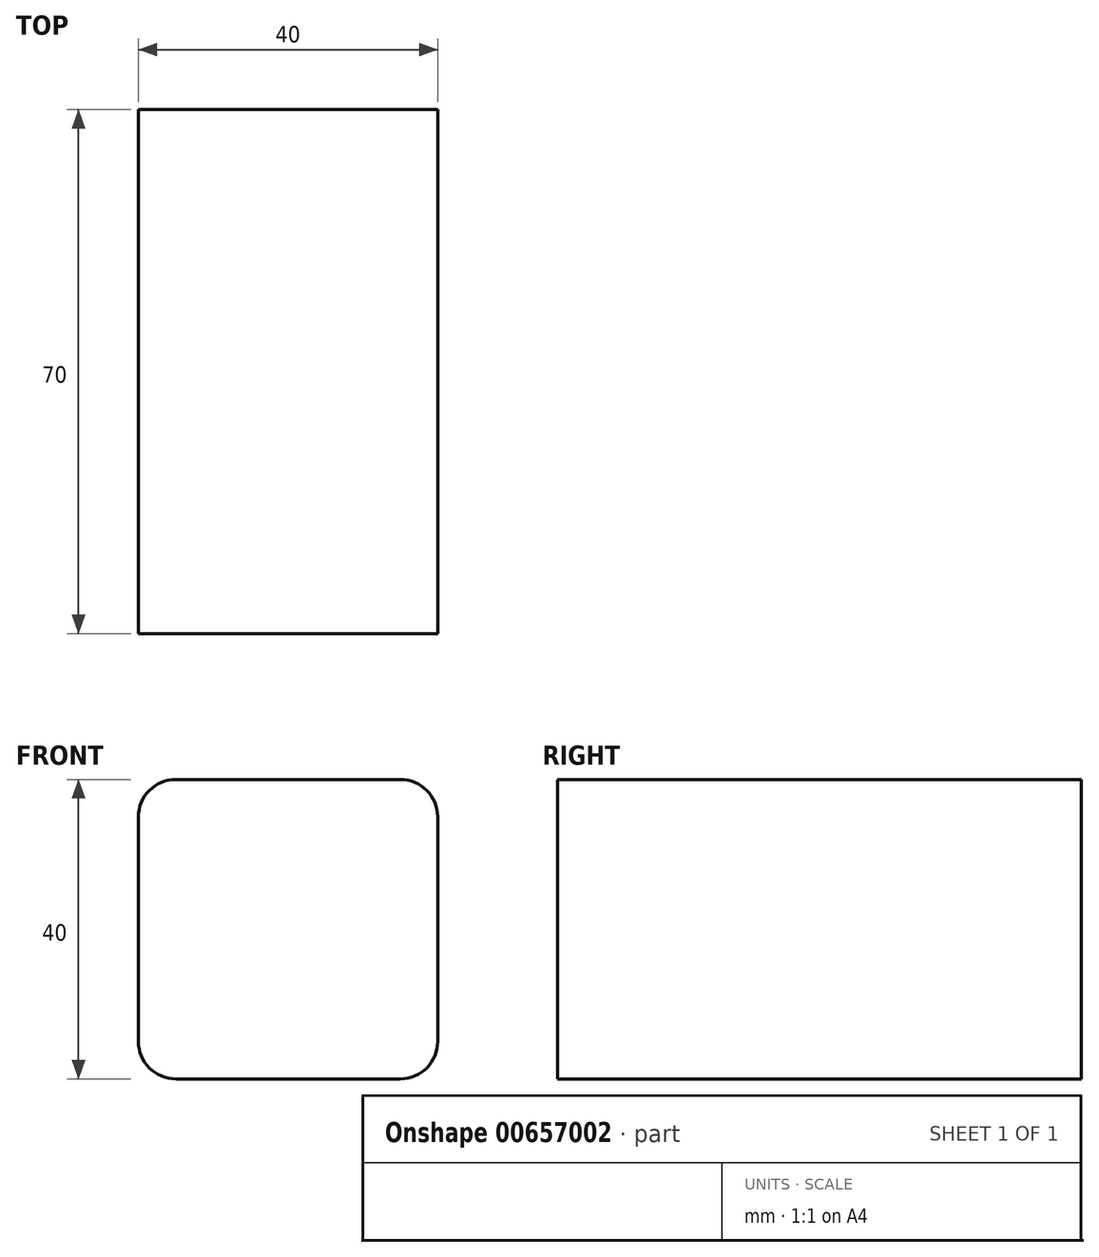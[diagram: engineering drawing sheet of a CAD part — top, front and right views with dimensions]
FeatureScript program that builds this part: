
annotation { "Feature Type Name" : "Feature", "Feature Type Description" : "" }
export const myFeature = defineFeature(function(context is Context, id is Id, definition is map)
    precondition{}
    {
        {
            var Q0;
            Q0=qCreatedBy(makeId("Front.planeOp"),FACE);
            var sketch = newSketch(context, id + "F0", { "sketchPlane" : qUnion([Q0])});
            skLineSegment(sketch, "E0.bottom", {"start": v(-63.38, 61.1) * mm, "end": v(-23.38, 61.1) * mm});
            skLineSegment(sketch, "E0.top", {"start": v(-63.38, 21.1) * mm, "end": v(-23.38, 21.1) * mm});
            skLineSegment(sketch, "E0.left", {"start": v(-63.38, 61.1) * mm, "end": v(-63.38, 21.1) * mm});
            skLineSegment(sketch, "E0.right", {"start": v(-23.38, 61.1) * mm, "end": v(-23.38, 21.1) * mm});
            skSolve(sketch);
        }
        {
            var Q0;
            Q0=makeQuery(id+"F0.imprint","IMPRINT",FACE,{"disambiguationData":[TD([[makeQuery(id+"F0.imprint","IMPRINT",EDGE,{"derivedFrom":sQuery(id+"F0.wireOp",EDGE,"E0.bottom")}),-1.0]])]});
            extrude(context, id + "F1", {"entities" : qUnion([Q0]), "depth" : 70 * mm, "offsetDistance" : 25.4 * mm});
        }
        {
            var Q0;
            Q0=makeQuery(id+"F1.opExtrude","SWEPT_EDGE",EDGE,{"disambiguationData":[OSD([sQuery(id+"F0.wireOp",EDGE,"E0.top"),sQuery(id+"F0.wireOp",EDGE,"E0.right")])]});
            var Q1;
            Q1=makeQuery(id+"F1.opExtrude","SWEPT_EDGE",EDGE,{"disambiguationData":[OSD([sQuery(id+"F0.wireOp",EDGE,"E0.bottom"),sQuery(id+"F0.wireOp",EDGE,"E0.right")])]});
            var Q2;
            Q2=makeQuery(id+"F1.opExtrude","SWEPT_EDGE",EDGE,{"disambiguationData":[OSD([sQuery(id+"F0.wireOp",EDGE,"E0.top"),sQuery(id+"F0.wireOp",EDGE,"E0.left")])]});
            var Q3;
            Q3=makeQuery(id+"F1.opExtrude","SWEPT_EDGE",EDGE,{"disambiguationData":[OSD([sQuery(id+"F0.wireOp",EDGE,"E0.bottom"),sQuery(id+"F0.wireOp",EDGE,"E0.left")])]});
            fillet(context, id + "F2", {"entities" : qUnion([Q0, Q1, Q2, Q3]), "radius" : 5 * mm, "tangentPropagation" : true, "allowEdgeOverflow" : false});
        }
    });
